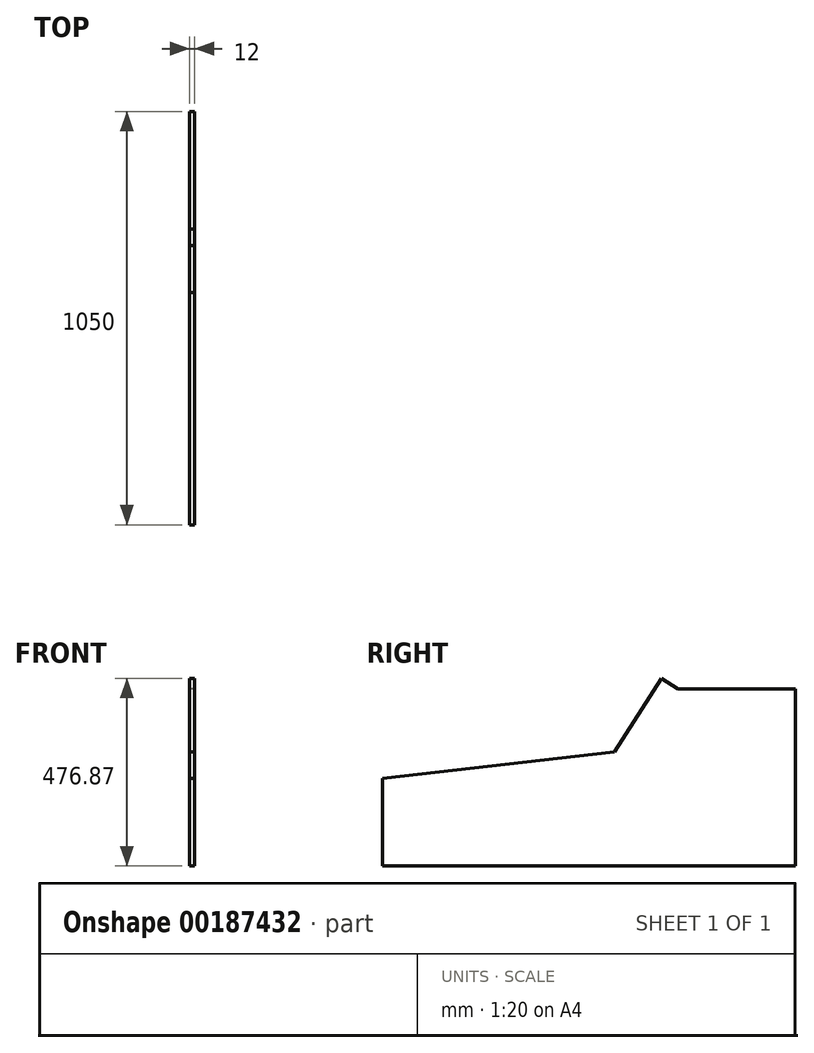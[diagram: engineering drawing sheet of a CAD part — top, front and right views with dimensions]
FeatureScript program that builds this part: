
annotation { "Feature Type Name" : "Feature", "Feature Type Description" : "" }
export const myFeature = defineFeature(function(context is Context, id is Id, definition is map)
    precondition{}
    {
        {
            var Q0;
            Q0=qCreatedBy(makeId("Right.planeOp"),FACE);
            var sketch = newSketch(context, id + "F0", { "sketchPlane" : qUnion([Q0])});
            skLineSegment(sketch, "E0.bottom", {"start": v(0, 0) * mm, "end": v(-738, 0) * mm});
            skLineSegment(sketch, "E0.top", {"start": v(0, 460) * mm, "end": v(-738, 460) * mm});
            skLineSegment(sketch, "E0.left", {"start": v(0, 0) * mm, "end": v(0, 460) * mm});
            skLineSegment(sketch, "E0.right", {"start": v(-738, 0) * mm, "end": v(-738, 460) * mm});
            skLineSegment(sketch, "E1", {"start": v(-100.56, 446.57) * mm, "end": v(-230.57, 242.52) * mm});
            skLineSegment(sketch, "E2", {"start": v(-230.57, 242.52) * mm, "end": v(-738, 185) * mm});
            skLineSegment(sketch, "E3", {"start": v(-100.56, 446.57) * mm, "end": v(-92, 460) * mm});
            skLineSegment(sketch, "E4.bottom", {"start": v(0, 0) * mm, "end": v(200, 0) * mm});
            skLineSegment(sketch, "E4.top", {"start": v(0, 460) * mm, "end": v(200, 460) * mm});
            skLineSegment(sketch, "E4.right", {"start": v(200, 0) * mm, "end": v(200, 460) * mm});
            skLineSegment(sketch, "E5", {"start": v(-738, 134.68) * mm, "end": v(-63.78, 211.1) * mm});
            skLineSegment(sketch, "E6", {"start": v(-32.71, 460) * mm, "end": v(-265.98, 93.9) * mm});
            skSolve(sketch);
        }
        {
            var Q0;
            {var subQ4=sQuery(id+"F0.wireOp",EDGE,"E0.left");Q0=makeQuery(id+"F0.imprint","IMPRINT",FACE,{"disambiguationData":[TD([[makeQuery(id+"F0.imprint","IMPRINT",EDGE,{"derivedFrom":subQ4}),1.0]])]});}
            var Q1;
            {var subQ5=sQuery(id+"F0.wireOp",EDGE,"E2");Q1=makeQuery(id+"F0.imprint","IMPRINT",FACE,{"disambiguationData":[TD([[makeQuery(id+"F0.imprint","IMPRINT",EDGE,{"derivedFrom":subQ5}),1.0]])]});}
            var Q2;
            {var subQ0=sQuery(id+"F0.wireOp",EDGE,"E1");Q2=makeQuery(id+"F0.imprint","IMPRINT",FACE,{"disambiguationData":[TD([[makeQuery(id+"F0.imprint","IMPRINT",EDGE,{"derivedFrom":subQ0}),1.0]])]});}
            var Q3;
            Q3=makeQuery(id+"F0.imprint","IMPRINT",FACE,{"disambiguationData":[TD([[makeQuery(id+"F0.imprint","IMPRINT",EDGE,{"derivedFrom":sQuery(id+"F0.wireOp",EDGE,"E4.bottom")}),1.0]])]});
            var Q4;
            {var subQ2=sQuery(id+"F0.wireOp",EDGE,"E0.bottom");Q4=makeQuery(id+"F0.imprint","IMPRINT",FACE,{"disambiguationData":[TD([[makeQuery(id+"F0.imprint","IMPRINT",EDGE,{"derivedFrom":subQ2}),-1.0]])]});}
            extrude(context, id + "F1", {"entities" : qUnion([Q0, Q1, Q2, Q3, Q4]), "depth" : 12 * mm});
        }
        {
            var Q0;
            {var subQ1=sQuery(id+"F0.wireOp",EDGE,"E4.top");var subQ7=sQuery(id+"F0.wireOp",EDGE,"E0.top");Q0=makeQuery(id+"FBUcGjjAI2LiSTe_1.boolean.opBoolean","SPLIT",FACE,{"disambiguationData":[TD([makeQuery(id+"FBUcGjjAI2LiSTe_1.opExtrude","SWEPT_FACE",FACE,{"disambiguationData":[OSD([sQuery(id+"FRhffPsowHkM5zk_1.wireOp",EDGE,"Yx9pkm1G-mTbN-YIqc-lDdE-2p7qJF1BQNZ1.left")])]})])],"derivedFrom":makeQuery(id+"F1.opExtrude","SWEPT_FACE",FACE,{"disambiguationData":[OSD([subQ7,subQ1])]})});}
            var Q1;
            {var subQ1=sQuery(id+"F0.wireOp",EDGE,"E4.top");var subQ7=sQuery(id+"F0.wireOp",EDGE,"E0.top");Q1=makeQuery(id+"FBUcGjjAI2LiSTe_1.boolean.opBoolean","SPLIT",FACE,{"disambiguationData":[TD([makeQuery(id+"FBUcGjjAI2LiSTe_1.opExtrude","SWEPT_FACE",FACE,{"disambiguationData":[OSD([sQuery(id+"FRhffPsowHkM5zk_1.wireOp",EDGE,"OsTsnuoV-NSr9-Tp8u-wZkD-H3Jly8ttqVjt.right")])]})])],"derivedFrom":makeQuery(id+"F1.opExtrude","SWEPT_FACE",FACE,{"disambiguationData":[OSD([subQ7,subQ1])]})});}
            var Q2;
            {var subQ0=sQuery(id+"F0.wireOp",EDGE,"E4.right");var subQ1=sQuery(id+"F0.wireOp",EDGE,"E4.top");var subQ7=sQuery(id+"F0.wireOp",EDGE,"E0.top");Q2=makeQuery(id+"FBUcGjjAI2LiSTe_1.boolean.opBoolean","SPLIT",FACE,{"disambiguationData":[TD([makeQuery(id+"F1.opExtrude","SWEPT_FACE",FACE,{"disambiguationData":[OSD([subQ0])]})])],"derivedFrom":makeQuery(id+"F1.opExtrude","SWEPT_FACE",FACE,{"disambiguationData":[OSD([subQ7,subQ1])]})});}
            extrude(context, id + "F2", {"entities" : qUnion([Q0, Q1, Q2]), "operationType" : NewBodyOperationType.REMOVE, "oppositeDirection" : true, "depth" : 10 * mm, "offsetDistance" : 25 * mm});
        }
        {
            var Q0;
            Q0=makeQuery(id+"F2.boolean.opBoolean","COPY",FACE,{"derivedFrom":makeQuery(id+"F2.opExtrude","SWEPT_FACE",FACE,{"disambiguationData":[OSD([sQuery(id+"F0.wireOp",EDGE,"E0.top"),sQuery(id+"F0.wireOp",EDGE,"E3")])]})});
            extrude(context, id + "F3", {"entities" : qUnion([Q0]), "operationType" : NewBodyOperationType.REMOVE, "oppositeDirection" : true, "depth" : 25 * mm, "offsetDistance" : 25 * mm});
        }
        {
            var Q0;
            Q0=makeQuery(id+"F1.opExtrude","CAP_FACE",FACE,{"disambiguationData":[OSD([sQuery(id+"F0.wireOp",EDGE,"E0.bottom"),sQuery(id+"F0.wireOp",EDGE,"E0.top"),sQuery(id+"F0.wireOp",EDGE,"E0.right"),sQuery(id+"F0.wireOp",EDGE,"E1"),sQuery(id+"F0.wireOp",EDGE,"E2"),sQuery(id+"F0.wireOp",EDGE,"E3"),sQuery(id+"F0.wireOp",EDGE,"E4.bottom"),sQuery(id+"F0.wireOp",EDGE,"E4.top"),sQuery(id+"F0.wireOp",EDGE,"E4.right")])],"isStart":true});
            var sketch = newSketch(context, id + "F4", { "sketchPlane" : qUnion([Q0])});
            skLineSegment(sketch, "E7", {"start": v(738, 185) * mm, "end": v(743.63, 234.68) * mm});
            skLineSegment(sketch, "E8", {"start": v(98.37, 450) * mm, "end": v(140.54, 476.87) * mm});
            skLineSegment(sketch, "E9", {"start": v(140.54, 476.87) * mm, "end": v(259.91, 289.52) * mm});
            skLineSegment(sketch, "E10", {"start": v(743.63, 234.68) * mm, "end": v(259.91, 289.52) * mm});
            skSolve(sketch);
        }
        {
            var Q0;
            Q0 = qSketchRegion(id + "F4", true);
            var Q1;
            Q1=makeQuery(id+"F4.imprint","IMPRINT",FACE,{"disambiguationData":[TD([[makeQuery(id+"F4.imprint","IMPRINT",EDGE,{"derivedFrom":sQuery(id+"F4.wireOp",EDGE,"E7")}),1.0]])]});
            extrude(context, id + "F5", {"entities" : qUnion([Q0, Q1]), "operationType" : NewBodyOperationType.ADD, "oppositeDirection" : true, "depth" : 12 * mm, "offsetDistance" : 25 * mm});
        }
        {
            var Q0;
            {var subQ0=sQuery(id+"F0.wireOp",EDGE,"E3");var subQ1=sQuery(id+"F0.wireOp",EDGE,"E2");var subQ2=sQuery(id+"F0.wireOp",EDGE,"E1");Q0=makeQuery(id+"F5.boolean.opBoolean","MERGE",FACE,{"derivedFrom":[makeQuery(id+"F1.opExtrude","CAP_FACE",FACE,{"disambiguationData":[OSD([sQuery(id+"F0.wireOp",EDGE,"E0.bottom"),sQuery(id+"F0.wireOp",EDGE,"E0.top"),sQuery(id+"F0.wireOp",EDGE,"E0.right"),subQ2,subQ1,subQ0,sQuery(id+"F0.wireOp",EDGE,"E4.bottom"),sQuery(id+"F0.wireOp",EDGE,"E4.top"),sQuery(id+"F0.wireOp",EDGE,"E4.right")])],"isStart":true}),makeQuery(id+"F5.opExtrude","CAP_FACE",FACE,{"disambiguationData":[OSD([subQ2,subQ1,subQ0,sQuery(id+"F4.wireOp",EDGE,"E7"),sQuery(id+"F4.wireOp",EDGE,"E8"),sQuery(id+"F4.wireOp",EDGE,"E9"),sQuery(id+"F4.wireOp",EDGE,"E10")])],"isStart":true})]});}
            var sketch = newSketch(context, id + "F6", { "sketchPlane" : qUnion([Q0])});
            skLineSegment(sketch, "E11", {"start": v(743.63, 234.68) * mm, "end": v(850, 222.62) * mm});
            skLineSegment(sketch, "E12", {"start": v(850, 222.62) * mm, "end": v(850, 0) * mm});
            skLineSegment(sketch, "E13", {"start": v(850, 0) * mm, "end": v(738, 0) * mm});
            skSolve(sketch);
        }
        {
            var Q0;
            Q0 = qSketchRegion(id + "F6", true);
            var Q1;
            Q1=makeQuery(id+"F6.imprint","IMPRINT",FACE,{"disambiguationData":[TD([[makeQuery(id+"F6.imprint","IMPRINT",EDGE,{"derivedFrom":sQuery(id+"F6.wireOp",EDGE,"E11")}),-1.0]])]});
            extrude(context, id + "F7", {"entities" : qUnion([Q0, Q1]), "operationType" : NewBodyOperationType.ADD, "oppositeDirection" : true, "depth" : 12 * mm, "offsetDistance" : 25 * mm});
        }
    });
